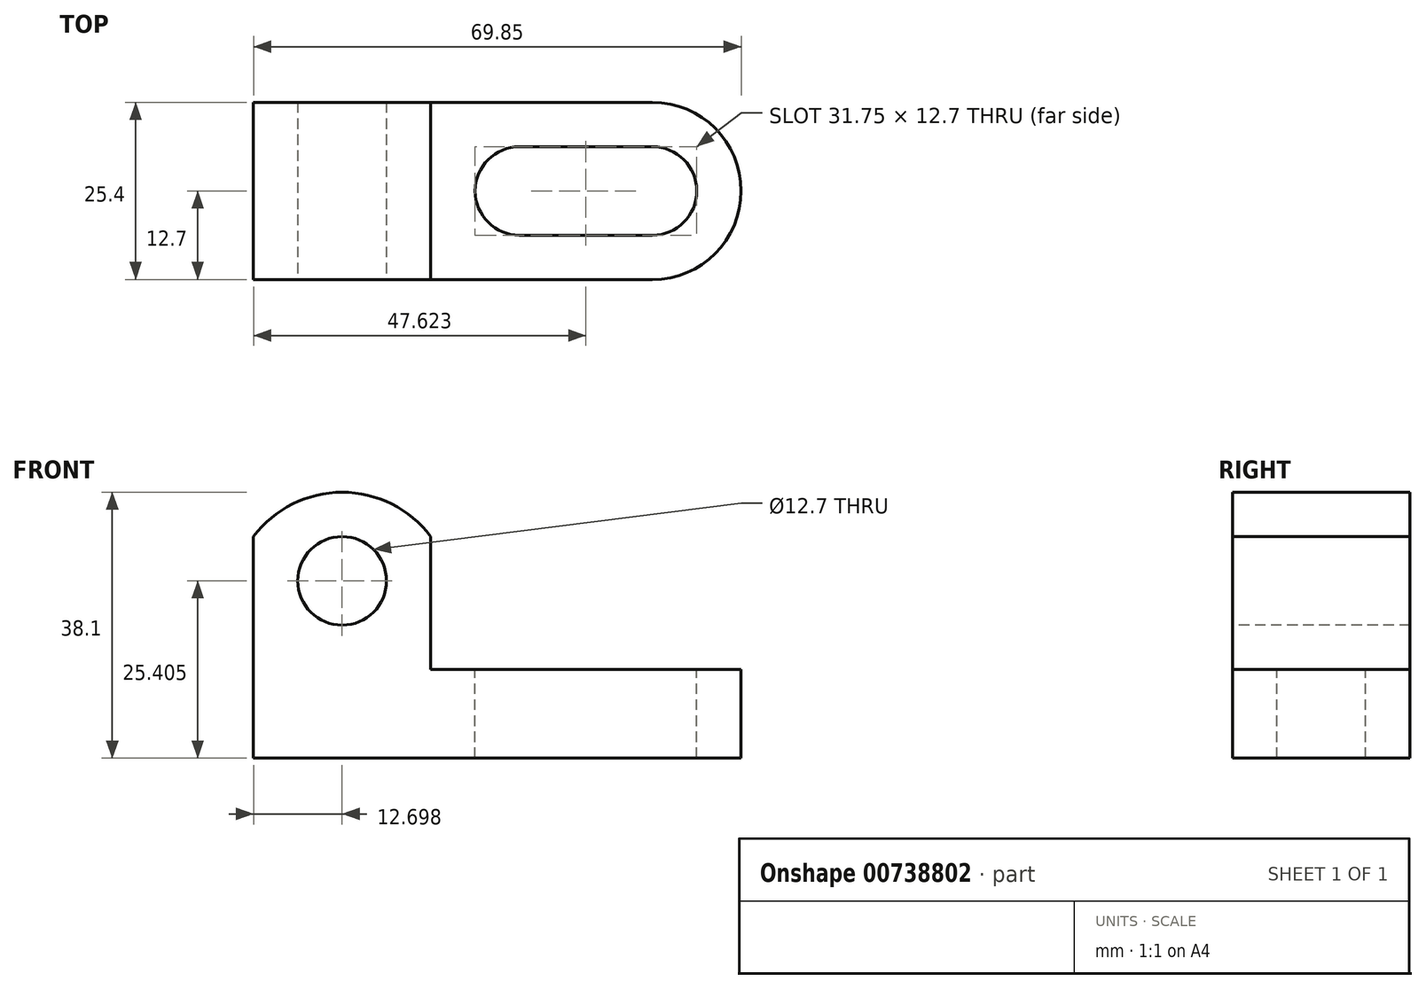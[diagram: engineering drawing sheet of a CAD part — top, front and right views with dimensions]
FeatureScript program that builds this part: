
annotation { "Feature Type Name" : "Feature", "Feature Type Description" : "" }
export const myFeature = defineFeature(function(context is Context, id is Id, definition is map)
    precondition{}
    {
        {
            var Q0;
            Q0=qCreatedBy(makeId("Front.planeOp"),FACE);
            var sketch = newSketch(context, id + "F0", { "sketchPlane" : qUnion([Q0])});
            skLineSegment(sketch, "E0.bottom", {"start": v(-38.34, 30.11) * mm, "end": v(31.5, 30.11) * mm});
            skLineSegment(sketch, "E0.top", {"start": v(-38.34, -7.99) * mm, "end": v(31.5, -7.99) * mm});
            skLineSegment(sketch, "E0.left", {"start": v(-38.34, 30.11) * mm, "end": v(-38.34, -7.99) * mm});
            skLineSegment(sketch, "E0.right", {"start": v(31.5, 30.11) * mm, "end": v(31.5, -7.99) * mm});
            skSolve(sketch);
        }
        {
            var Q0;
            Q0 = qSketchRegion(id + "F0", true);
            extrude(context, id + "F1", {"entities" : qUnion([Q0]), "depth" : 25.4 * mm, "offsetDistance" : 25.4 * mm});
        }
        {
            var Q0;
            Q0=makeQuery(id+"F1.opExtrude","CAP_FACE",FACE,{"disambiguationData":[OSD([sQuery(id+"F0.wireOp",EDGE,"E0.bottom"),sQuery(id+"F0.wireOp",EDGE,"E0.top"),sQuery(id+"F0.wireOp",EDGE,"E0.left"),sQuery(id+"F0.wireOp",EDGE,"E0.right")])],"isStart":false});
            var sketch = newSketch(context, id + "F2", { "sketchPlane" : qUnion([Q0])});
            skLineSegment(sketch, "E1", {"start": v(-12.94, 30.11) * mm, "end": v(-12.94, 4.71) * mm});
            skLineSegment(sketch, "E2", {"start": v(-12.94, 4.71) * mm, "end": v(31.5, 4.71) * mm});
            skSolve(sketch);
        }
        {
            var Q0;
            Q0 = qSketchRegion(id + "F2", true);
            var Q1;
            {var subQ0=sQuery(id+"F2.wireOp",EDGE,"E1");Q1=makeQuery(id+"F2.imprint","IMPRINT",FACE,{"disambiguationData":[TD([[makeQuery(id+"F2.imprint","IMPRINT",EDGE,{"derivedFrom":subQ0}),1.0]])]});}
            extrude(context, id + "F3", {"entities" : qUnion([Q0, Q1]), "operationType" : NewBodyOperationType.REMOVE, "endBound" : BoundingType.THROUGH_ALL, "oppositeDirection" : true, "depth" : 25.4 * mm, "offsetDistance" : 25.4 * mm});
        }
        {
            var Q0;
            Q0=makeQuery(id+"F1.opExtrude","CAP_FACE",FACE,{"disambiguationData":[OSD([sQuery(id+"F0.wireOp",EDGE,"E0.bottom"),sQuery(id+"F0.wireOp",EDGE,"E0.top"),sQuery(id+"F0.wireOp",EDGE,"E0.left"),sQuery(id+"F0.wireOp",EDGE,"E0.right")])],"isStart":false});
            var sketch = newSketch(context, id + "F4", { "sketchPlane" : qUnion([Q0])});
            skLineSegment(sketch, "E3", {"start": v(-38.34, 23.76) * mm, "end": v(-12.94, 23.76) * mm});
            skLineSegment(sketch, "E4", {"start": v(-38.34, 11.06) * mm, "end": v(-12.94, 11.06) * mm});
            skLineSegment(sketch, "E5", {"start": v(-32, 30.11) * mm, "end": v(-32, -7.99) * mm});
            skLineSegment(sketch, "E6", {"start": v(-19.3, 30.11) * mm, "end": v(-19.3, -7.99) * mm});
            skCircle(sketch, "E7", {"center": v(-25.64, 17.41) * mm, "radius": 6.35 * mm});
            skArc(sketch, "E8", {"start": v(-12.94, 23.76) * mm, "mid": v(-25.64, 30.11) * mm, "end": v(-38.34, 23.76) * mm});
            skSolve(sketch);
        }
        {
            var Q0;
            {var subQ0=sQuery(id+"F4.wireOp",EDGE,"E6");var subQ1=makeQuery(id+"F1.opExtrude","CAP_EDGE",EDGE,{"disambiguationData":[OSD([sQuery(id+"F0.wireOp",EDGE,"E0.bottom")])],"isStart":false});var subQ2=makeQuery(id+"F4.imprint","INTERSECT",VERTEX,{"derivedFrom":[subQ1,subQ0]});Q0=makeQuery(id+"F4.imprint","IMPRINT",FACE,{"disambiguationData":[TD([[makeQuery(id+"F4.imprint","IMPRINT",EDGE,{"disambiguationData":[TD([[subQ2,-1.0]])],"derivedFrom":subQ0}),1.0]])]});}
            var Q1;
            {var subQ0=sQuery(id+"F4.wireOp",EDGE,"E5");var subQ1=makeQuery(id+"F1.opExtrude","CAP_EDGE",EDGE,{"disambiguationData":[OSD([sQuery(id+"F0.wireOp",EDGE,"E0.bottom")])],"isStart":false});var subQ2=makeQuery(id+"F4.imprint","INTERSECT",VERTEX,{"derivedFrom":[subQ1,subQ0]});Q1=makeQuery(id+"F4.imprint","IMPRINT",FACE,{"disambiguationData":[TD([[makeQuery(id+"F4.imprint","IMPRINT",EDGE,{"disambiguationData":[TD([[subQ2,-1.0]])],"derivedFrom":subQ0}),-1.0]])]});}
            var Q2;
            {var subQ0=sQuery(id+"F4.wireOp",EDGE,"E7");var subQ1=makeQuery(id+"F4.imprint","INTERSECT",VERTEX,{"derivedFrom":[sQuery(id+"F4.wireOp",EDGE,"E3"),subQ0]});Q2=makeQuery(id+"F4.imprint","IMPRINT",FACE,{"disambiguationData":[TD([[makeQuery(id+"F4.imprint","IMPRINT",EDGE,{"disambiguationData":[TD([[subQ1,1.0]])],"derivedFrom":subQ0}),1.0]])]});}
            var Q3;
            {var subQ0=sQuery(id+"F4.wireOp",EDGE,"E6");var subQ1=makeQuery(id+"F1.opExtrude","CAP_EDGE",EDGE,{"disambiguationData":[OSD([sQuery(id+"F0.wireOp",EDGE,"E0.bottom")])],"isStart":false});var subQ2=makeQuery(id+"F4.imprint","INTERSECT",VERTEX,{"derivedFrom":[subQ1,subQ0]});Q3=makeQuery(id+"F4.imprint","IMPRINT",FACE,{"disambiguationData":[TD([[makeQuery(id+"F4.imprint","IMPRINT",EDGE,{"disambiguationData":[TD([[subQ2,-1.0]])],"derivedFrom":subQ0}),-1.0]])]});}
            var Q4;
            {var subQ0=sQuery(id+"F4.wireOp",EDGE,"E5");var subQ1=makeQuery(id+"F1.opExtrude","CAP_EDGE",EDGE,{"disambiguationData":[OSD([sQuery(id+"F0.wireOp",EDGE,"E0.bottom")])],"isStart":false});var subQ2=makeQuery(id+"F4.imprint","INTERSECT",VERTEX,{"derivedFrom":[subQ1,subQ0]});Q4=makeQuery(id+"F4.imprint","IMPRINT",FACE,{"disambiguationData":[TD([[makeQuery(id+"F4.imprint","IMPRINT",EDGE,{"disambiguationData":[TD([[subQ2,-1.0]])],"derivedFrom":subQ0}),1.0]])]});}
            extrude(context, id + "F5", {"entities" : qUnion([Q0, Q1, Q2, Q3, Q4]), "operationType" : NewBodyOperationType.REMOVE, "endBound" : BoundingType.THROUGH_ALL, "oppositeDirection" : true, "depth" : 25.4 * mm, "offsetDistance" : 25.4 * mm});
        }
        {
            var Q0;
            Q0=makeQuery(id+"F3.boolean.opBoolean","COPY",FACE,{"derivedFrom":makeQuery(id+"F3.opExtrude","SWEPT_FACE",FACE,{"disambiguationData":[OSD([sQuery(id+"F2.wireOp",EDGE,"E2")])]})});
            var sketch = newSketch(context, id + "F6", { "sketchPlane" : qUnion([Q0])});
            skLineSegment(sketch, "E9", {"start": v(-0.24, 0) * mm, "end": v(-0.24, -25.4) * mm});
            skLineSegment(sketch, "E10", {"start": v(18.8, 0) * mm, "end": v(18.8, -25.4) * mm});
            skLineSegment(sketch, "E11", {"start": v(-12.94, -6.35) * mm, "end": v(31.5, -6.35) * mm});
            skLineSegment(sketch, "E12", {"start": v(-12.94, -19.05) * mm, "end": v(31.5, -19.05) * mm});
            skCircle(sketch, "E13", {"center": v(-0.24, -12.7) * mm, "radius": 6.35 * mm});
            skCircle(sketch, "E14", {"center": v(18.8, -12.7) * mm, "radius": 6.35 * mm});
            skArc(sketch, "E15", {"start": v(18.8, -25.4) * mm, "mid": v(31.5, -12.7) * mm, "end": v(18.8, 0) * mm});
            skSolve(sketch);
        }
        {
            var Q0;
            {var subQ0=sQuery(id+"F6.wireOp",EDGE,"E13");var subQ1=sQuery(id+"F6.wireOp",EDGE,"E9");var subQ2=makeQuery(id+"F6.imprint","INTERSECT",VERTEX,{"derivedFrom":[subQ1,sQuery(id+"F6.wireOp",EDGE,"E11"),subQ0]});Q0=makeQuery(id+"F6.imprint","IMPRINT",FACE,{"disambiguationData":[TD([[makeQuery(id+"F6.imprint","IMPRINT",EDGE,{"disambiguationData":[TD([[subQ2,-1.0]])],"derivedFrom":subQ1}),1.0]])]});}
            var Q1;
            {var subQ0=sQuery(id+"F6.wireOp",EDGE,"E14");var subQ1=sQuery(id+"F6.wireOp",EDGE,"E10");var subQ2=makeQuery(id+"F6.imprint","INTERSECT",VERTEX,{"derivedFrom":[subQ1,sQuery(id+"F6.wireOp",EDGE,"E11"),subQ0]});Q1=makeQuery(id+"F6.imprint","IMPRINT",FACE,{"disambiguationData":[TD([[makeQuery(id+"F6.imprint","IMPRINT",EDGE,{"disambiguationData":[TD([[subQ2,-1.0]])],"derivedFrom":subQ1}),-1.0]])]});}
            var Q2;
            {var subQ0=sQuery(id+"F6.wireOp",EDGE,"E14");var subQ1=sQuery(id+"F6.wireOp",EDGE,"E10");var subQ2=makeQuery(id+"F6.imprint","INTERSECT",VERTEX,{"derivedFrom":[subQ1,sQuery(id+"F6.wireOp",EDGE,"E11"),subQ0]});Q2=makeQuery(id+"F6.imprint","IMPRINT",FACE,{"disambiguationData":[TD([[makeQuery(id+"F6.imprint","IMPRINT",EDGE,{"disambiguationData":[TD([[subQ2,-1.0]])],"derivedFrom":subQ1}),1.0]])]});}
            var Q3;
            {var subQ0=sQuery(id+"F6.wireOp",EDGE,"E13");var subQ1=sQuery(id+"F6.wireOp",EDGE,"E11");var subQ2=sQuery(id+"F6.wireOp",EDGE,"E9");var subQ3=makeQuery(id+"F6.imprint","INTERSECT",VERTEX,{"derivedFrom":[subQ2,subQ1,subQ0]});Q3=makeQuery(id+"F6.imprint","IMPRINT",FACE,{"disambiguationData":[TD([[makeQuery(id+"F6.imprint","IMPRINT",EDGE,{"disambiguationData":[TD([[subQ3,-1.0]])],"derivedFrom":subQ1}),-1.0]])]});}
            var Q4;
            {var subQ0=sQuery(id+"F6.wireOp",EDGE,"E11");var subQ5=sQuery(id+"F6.wireOp",EDGE,"E15");var subQ6=makeQuery(id+"F6.imprint","INTERSECT",VERTEX,{"derivedFrom":[subQ0,subQ5]});Q4=makeQuery(id+"F6.imprint","IMPRINT",FACE,{"disambiguationData":[TD([[makeQuery(id+"F6.imprint","IMPRINT",EDGE,{"disambiguationData":[TD([[subQ6,-1.0]])],"derivedFrom":subQ0}),1.0]])]});}
            var Q5;
            {var subQ0=sQuery(id+"F6.wireOp",EDGE,"E12");var subQ4=sQuery(id+"F6.wireOp",EDGE,"E15");var subQ5=makeQuery(id+"F6.imprint","INTERSECT",VERTEX,{"derivedFrom":[subQ0,subQ4]});Q5=makeQuery(id+"F6.imprint","IMPRINT",FACE,{"disambiguationData":[TD([[makeQuery(id+"F6.imprint","IMPRINT",EDGE,{"disambiguationData":[TD([[subQ5,-1.0]])],"derivedFrom":subQ0}),-1.0]])]});}
            var Q6;
            {var subQ0=sQuery(id+"F6.wireOp",EDGE,"E12");var subQ3=sQuery(id+"F6.wireOp",EDGE,"E15");var subQ4=makeQuery(id+"F6.imprint","INTERSECT",VERTEX,{"derivedFrom":[subQ0,subQ3]});Q6=makeQuery(id+"F6.imprint","IMPRINT",FACE,{"disambiguationData":[TD([[makeQuery(id+"F6.imprint","IMPRINT",EDGE,{"disambiguationData":[TD([[subQ4,-1.0]])],"derivedFrom":subQ0}),1.0]])]});}
            var Q7;
            {var subQ0=sQuery(id+"F6.wireOp",EDGE,"E11");var subQ3=sQuery(id+"F6.wireOp",EDGE,"E15");var subQ4=makeQuery(id+"F6.imprint","INTERSECT",VERTEX,{"derivedFrom":[subQ0,subQ3]});Q7=makeQuery(id+"F6.imprint","IMPRINT",FACE,{"disambiguationData":[TD([[makeQuery(id+"F6.imprint","IMPRINT",EDGE,{"disambiguationData":[TD([[subQ4,-1.0]])],"derivedFrom":subQ0}),-1.0]])]});}
            var Q8;
            {var subQ0=sQuery(id+"F6.wireOp",EDGE,"E13");var subQ1=sQuery(id+"F6.wireOp",EDGE,"E9");var subQ2=makeQuery(id+"F6.imprint","INTERSECT",VERTEX,{"derivedFrom":[subQ1,sQuery(id+"F6.wireOp",EDGE,"E11"),subQ0]});Q8=makeQuery(id+"F6.imprint","IMPRINT",FACE,{"disambiguationData":[TD([[makeQuery(id+"F6.imprint","IMPRINT",EDGE,{"disambiguationData":[TD([[subQ2,-1.0]])],"derivedFrom":subQ1}),-1.0]])]});}
            extrude(context, id + "F7", {"entities" : qUnion([Q0, Q1, Q2, Q3, Q4, Q5, Q6, Q7, Q8]), "operationType" : NewBodyOperationType.REMOVE, "endBound" : BoundingType.THROUGH_ALL, "oppositeDirection" : true, "depth" : 25.4 * mm, "offsetDistance" : 25.4 * mm});
        }
    });
